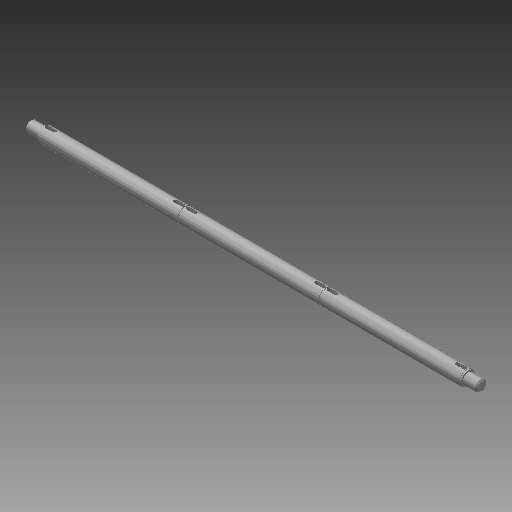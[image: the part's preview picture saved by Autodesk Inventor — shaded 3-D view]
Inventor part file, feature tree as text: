
AUTODESK INVENTOR PART (.ipt)
format: ipt  version: 2018 (Build 220112000, 112)  size: 202,752 bytes
history: native  units: mm
features: other x23, chamfer x2, revolve x1
ambient origin geometry x6: Origin, XZ Plane, XY Plane, X Axis, Y Axis, Z Axis
bodies: Solid1 (feature_tree)
feature tree (26):
  revolve  "Revolution1"  [1 undecoded]
  other  "Keyway4"
  other  "Keyway5"
  other  "Keyway6"
  other  "Keyway7"
  other  "Keyway2"
  other  "Keyway3"
  other  "Retaining Ring Groove4"
  other  "Retaining Ring Groove5"
  chamfer  "Chamfer2"  Distance=4.0mm
  other  "Retaining Ring Groove3"
  other  "Retaining Ring Groove2"
  chamfer  "Chamfer1"  Distance=5.5mm
  other  "Start Plane"
  other  "Origin point"
  other  "Main Sketch"
  other  "iFeature27:2"
  other  "iFeature27:3"
  other  "iFeature27:4"
  other  "iFeature27:5"
  other  "iFeature3:2"
  other  "iFeature3:3"
  other  "iFeature3:4"
  other  "iFeature3:5"
  other  "iFeature3:6"
  other  "iFeature3:7"
note: 1 required parameter value undecoded (feature->parameter linkage not recoverable at this tier; creation-order binding heuristic only, values carry confidence <= 0.55)
